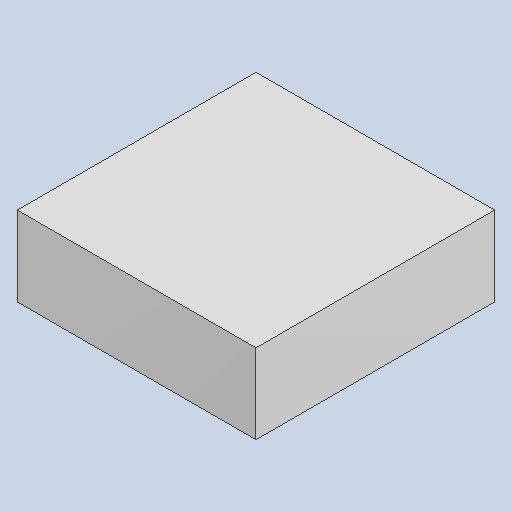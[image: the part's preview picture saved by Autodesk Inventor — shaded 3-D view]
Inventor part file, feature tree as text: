
AUTODESK INVENTOR PART (.ipt)
format: ipt  version: 2023.4 (Build 274418000, 418)  size: 79,872 bytes
history: native  units: mm
features: extrude x1
ambient origin geometry x8: Origin, YZ Plane, XZ Plane, XY Plane, X Axis, Y Axis, Z Axis, Center Point
bodies: Solid1 (feature_tree)
feature tree (1):
  extrude  "Extruded_30"  [1 undecoded]
note: 1 required parameter value undecoded (feature->parameter linkage not recoverable at this tier; creation-order binding heuristic only, values carry confidence <= 0.55)
